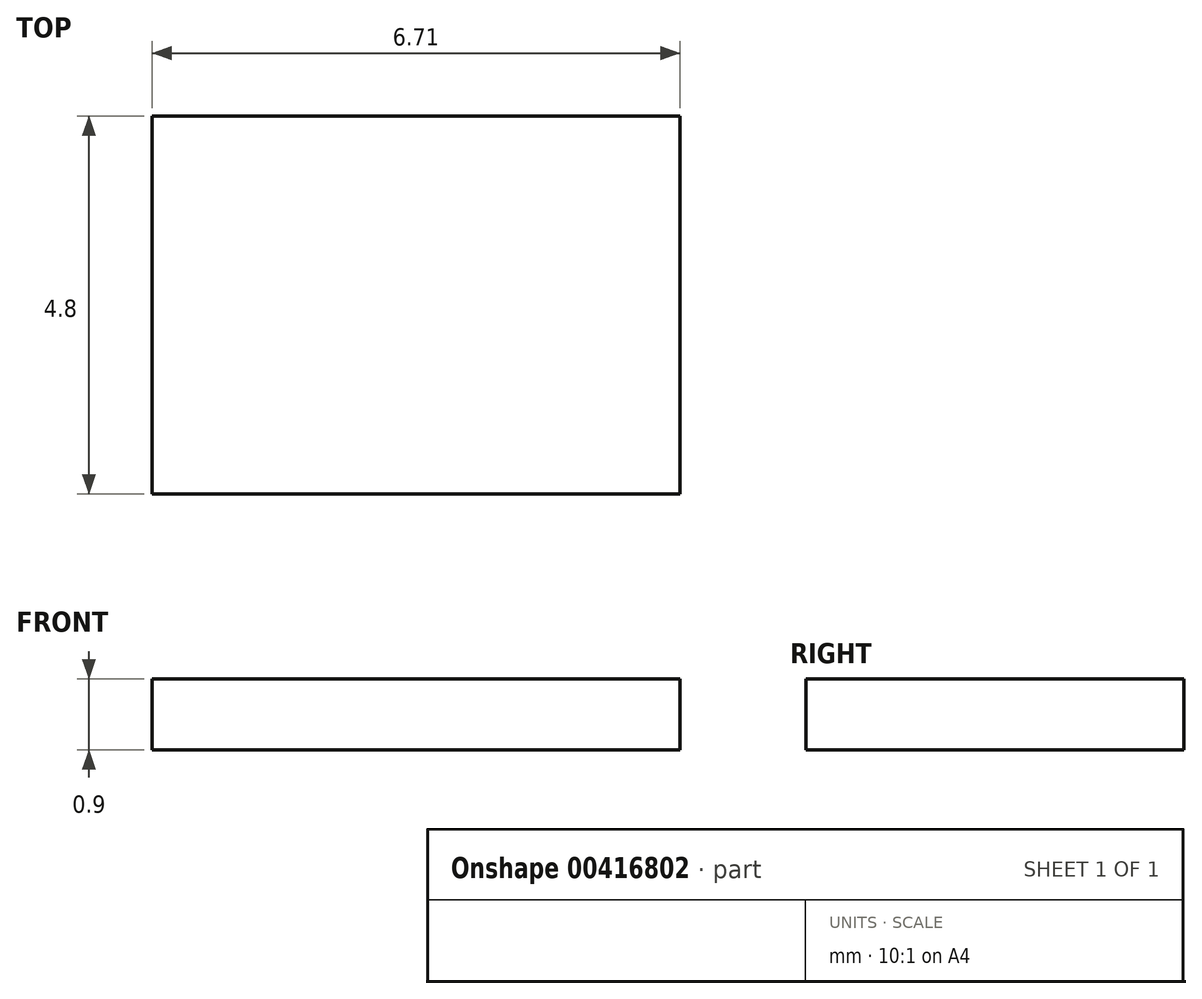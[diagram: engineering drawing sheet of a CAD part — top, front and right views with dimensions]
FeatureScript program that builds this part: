
annotation { "Feature Type Name" : "Feature", "Feature Type Description" : "" }
export const myFeature = defineFeature(function(context is Context, id is Id, definition is map)
    precondition{}
    {
        {
            var Q0;
            Q0=qCreatedBy(makeId("Top.planeOp"),FACE);
            var sketch = newSketch(context, id + "F0", { "sketchPlane" : qUnion([Q0])});
            skLineSegment(sketch, "E0.bottom", {"start": v(0, 0) * mm, "end": v(6.71, 0) * mm});
            skLineSegment(sketch, "E0.top", {"start": v(0, 4.8) * mm, "end": v(6.7, 4.8) * mm});
            skLineSegment(sketch, "E0.left", {"start": v(0, 0) * mm, "end": v(0, 4.8) * mm});
            skLineSegment(sketch, "E0.right", {"start": v(6.71, 0) * mm, "end": v(6.71, 4.8) * mm});
            skSolve(sketch);
        }
        {
            var Q0;
            Q0=makeQuery(id+"F0.imprint","IMPRINT",FACE,{"disambiguationData":[TD([[makeQuery(id+"F0.imprint","IMPRINT",EDGE,{"derivedFrom":sQuery(id+"F0.wireOp",EDGE,"E0.bottom")}),1.0]])]});
            extrude(context, id + "F1", {"entities" : qUnion([Q0]), "depth" : .9 * mm, "offsetDistance" : 25.4 * mm});
        }
    });
